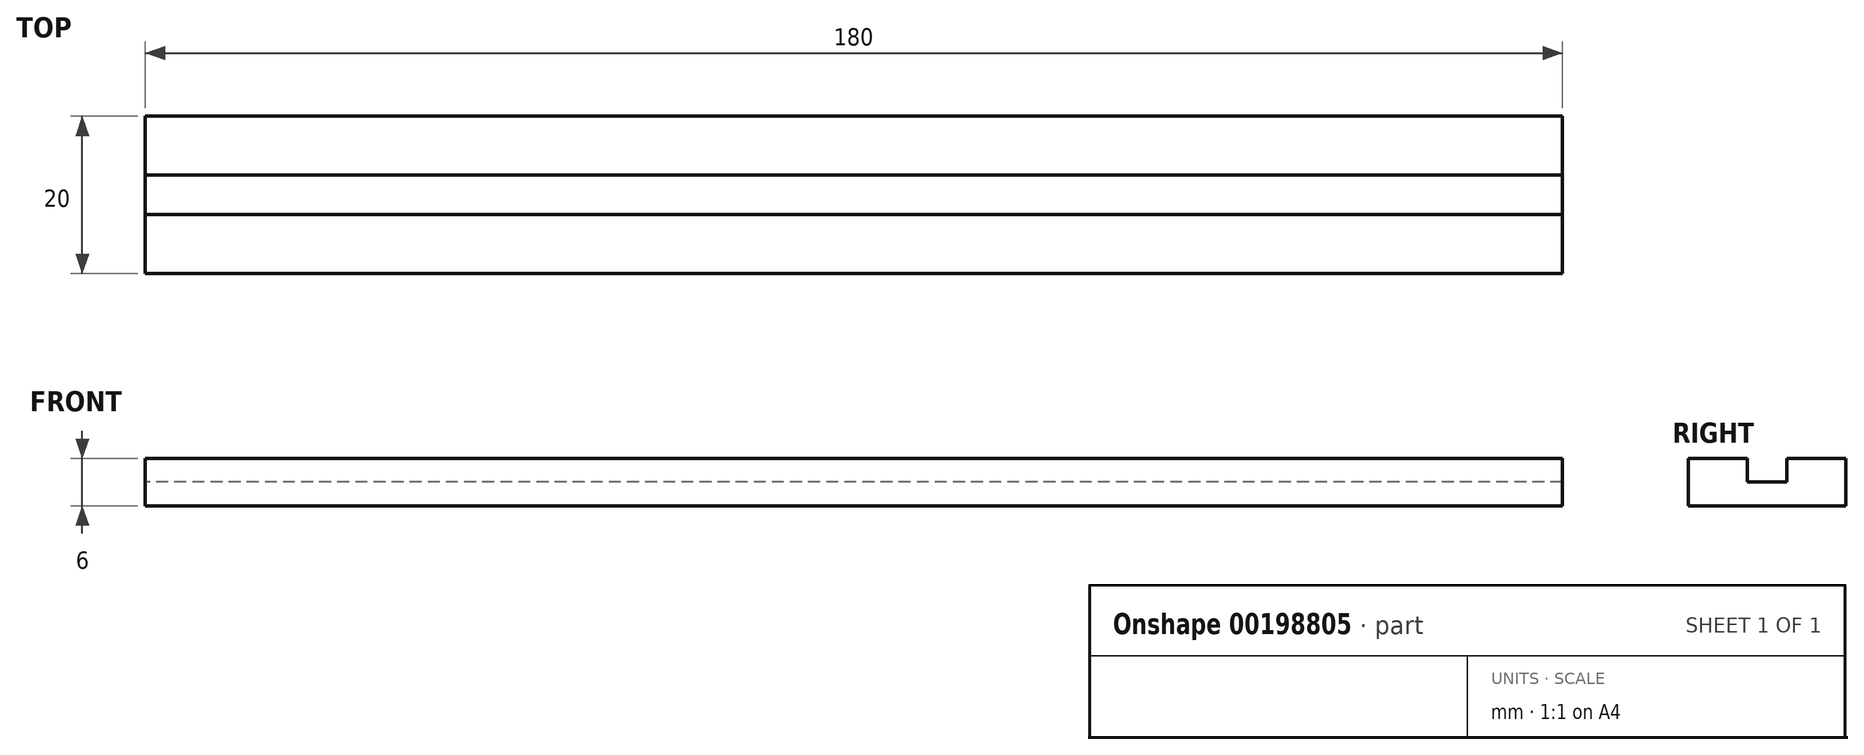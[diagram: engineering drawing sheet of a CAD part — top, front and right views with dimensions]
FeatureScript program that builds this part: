
annotation { "Feature Type Name" : "Feature", "Feature Type Description" : "" }
export const myFeature = defineFeature(function(context is Context, id is Id, definition is map)
    precondition{}
    {
        {
            var Q0;
            Q0=qCreatedBy(makeId("Right.planeOp"),FACE);
            var sketch = newSketch(context, id + "F0", { "sketchPlane" : qUnion([Q0])});
            skLineSegment(sketch, "E0", {"start": v(0, 0) * mm, "end": v(-10, 0) * mm});
            skLineSegment(sketch, "E1", {"start": v(-10, 0) * mm, "end": v(-10, 6) * mm});
            skLineSegment(sketch, "E2", {"start": v(-10, 6) * mm, "end": v(-2.5, 6) * mm});
            skLineSegment(sketch, "E3", {"start": v(-2.5, 6) * mm, "end": v(-2.5, 3) * mm});
            skLineSegment(sketch, "E4", {"start": v(-2.5, 3) * mm, "end": v(0, 3) * mm});
            skLineSegment(sketch, "E5", {"start": v(0, 3) * mm, "end": v(0, 0) * mm});
            skLineSegment(sketch, "E6", {"start": v(0, 23.09) * mm, "end": v(0, -25.12) * mm, "construction": true});
            skLineSegment(sketch, "E7.MirrorCS", {"start": v(10, 6) * mm, "end": v(2.5, 6) * mm});
            skLineSegment(sketch, "E8.MirrorCS", {"start": v(2.5, 3) * mm, "end": v(0, 3) * mm});
            skLineSegment(sketch, "E9.MirrorCS", {"start": v(2.5, 6) * mm, "end": v(2.5, 3) * mm});
            skLineSegment(sketch, "E10.MirrorCS", {"start": v(0, 0) * mm, "end": v(10, 0) * mm});
            skLineSegment(sketch, "E11.MirrorCS", {"start": v(10, 0) * mm, "end": v(10, 6) * mm});
            skSolve(sketch);
        }
        {
            var Q0;
            Q0 = qSketchRegion(id + "F0", true);
            extrude(context, id + "F1", {"entities" : qUnion([Q0]), "depth" : 180 * mm});
        }
    });
